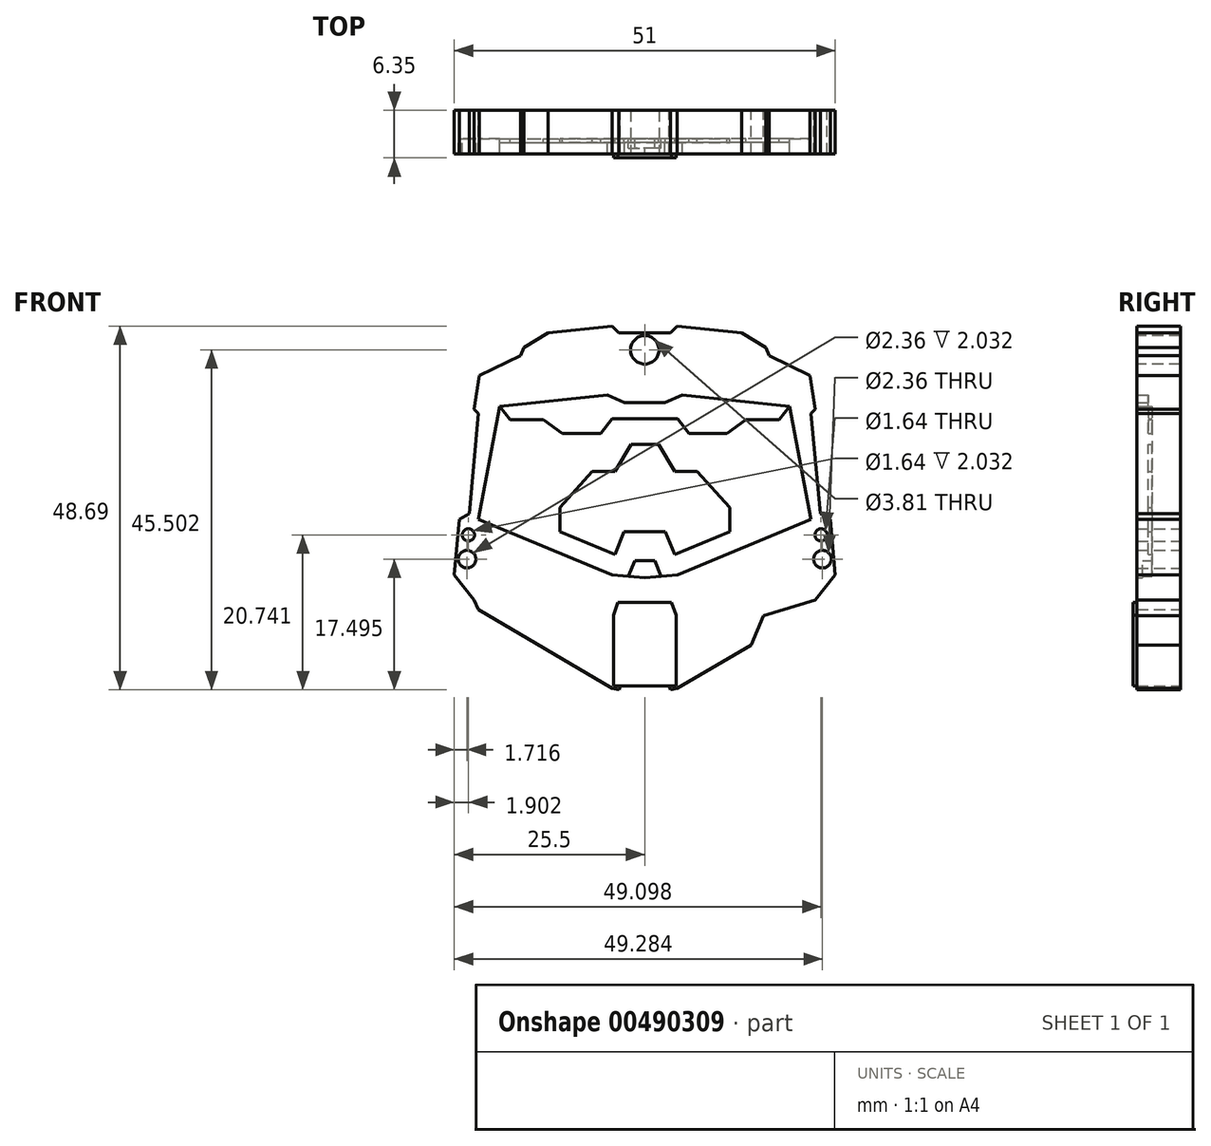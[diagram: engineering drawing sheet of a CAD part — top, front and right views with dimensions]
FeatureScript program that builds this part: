
annotation { "Feature Type Name" : "Feature", "Feature Type Description" : "" }
export const myFeature = defineFeature(function(context is Context, id is Id, definition is map)
    precondition{}
    {
        {
            var Q0;
            Q0=qCreatedBy(makeId("Front.planeOp"),FACE);
            var sketch = newSketch(context, id + "F0", { "sketchPlane" : qUnion([Q0])});
            skLineSegment(sketch, "E0", {"start": v(0, 26.6) * mm, "end": v(0, -24.2) * mm, "construction": true});
            skLineSegment(sketch, "E1", {"start": v(0, 26.6) * mm, "end": v(3.47, 26.6) * mm});
            skLineSegment(sketch, "E2", {"start": v(3.47, 26.6) * mm, "end": v(4.35, 27.52) * mm});
            skLineSegment(sketch, "E3", {"start": v(4.35, 27.52) * mm, "end": v(12.96, 26.6) * mm});
            skLineSegment(sketch, "E4", {"start": v(12.96, 26.6) * mm, "end": v(16.19, 24.61) * mm});
            skLineSegment(sketch, "E5", {"start": v(16.19, 24.61) * mm, "end": v(16.63, 23.54) * mm});
            skLineSegment(sketch, "E6", {"start": v(16.63, 23.54) * mm, "end": v(22.14, 20.88) * mm});
            skLineSegment(sketch, "E7", {"start": v(22.14, 20.88) * mm, "end": v(22.83, 16.39) * mm});
            skLineSegment(sketch, "E8", {"start": v(22.83, 16.39) * mm, "end": v(22.26, 15.82) * mm});
            skLineSegment(sketch, "E9", {"start": v(22.26, 15.82) * mm, "end": v(23.5, 2.4) * mm});
            skLineSegment(sketch, "E10", {"start": v(23.5, 2.4) * mm, "end": v(24.82, 1.66) * mm});
            skLineSegment(sketch, "E11", {"start": v(24.82, 1.66) * mm, "end": v(25.5, -5.75) * mm});
            skLineSegment(sketch, "E12", {"start": v(25.5, -5.75) * mm, "end": v(22.83, -9.12) * mm});
            skLineSegment(sketch, "E13", {"start": v(22.83, -9.12) * mm, "end": v(22.26, -10.43) * mm});
            skLineSegment(sketch, "E14", {"start": v(22.26, -10.43) * mm, "end": v(4.35, -20.92) * mm});
            skLineSegment(sketch, "E15", {"start": v(4.35, -20.92) * mm, "end": v(3.42, -21.17) * mm});
            skLineSegment(sketch, "E16", {"start": v(3.42, -21.17) * mm, "end": v(3.28, -20.63) * mm});
            skLineSegment(sketch, "E17", {"start": v(3.28, -20.63) * mm, "end": v(0, -20.63) * mm});
            skLineSegment(sketch, "E18.MirrorCS", {"start": v(-4.35, -20.92) * mm, "end": v(-3.42, -21.17) * mm});
            skLineSegment(sketch, "E19.MirrorCS", {"start": v(-3.42, -21.17) * mm, "end": v(-3.28, -20.63) * mm});
            skLineSegment(sketch, "E20.MirrorCS", {"start": v(-22.83, -9.12) * mm, "end": v(-22.26, -10.43) * mm});
            skLineSegment(sketch, "E21.MirrorCS", {"start": v(-23.5, 2.4) * mm, "end": v(-24.82, 1.66) * mm});
            skLineSegment(sketch, "E22.MirrorCS", {"start": v(-3.47, 26.6) * mm, "end": v(-4.35, 27.52) * mm});
            skLineSegment(sketch, "E23.MirrorCS", {"start": v(-16.19, 24.61) * mm, "end": v(-16.63, 23.54) * mm});
            skLineSegment(sketch, "E24.MirrorCS", {"start": v(-22.83, 16.39) * mm, "end": v(-22.26, 15.82) * mm});
            skLineSegment(sketch, "E25.MirrorCS", {"start": v(-22.26, -10.43) * mm, "end": v(-4.35, -20.92) * mm});
            skLineSegment(sketch, "E26.MirrorCS", {"start": v(-25.5, -5.75) * mm, "end": v(-22.83, -9.12) * mm});
            skLineSegment(sketch, "E27.MirrorCS", {"start": v(-24.82, 1.66) * mm, "end": v(-25.5, -5.75) * mm});
            skLineSegment(sketch, "E28.MirrorCS", {"start": v(-22.26, 15.82) * mm, "end": v(-23.5, 2.4) * mm});
            skLineSegment(sketch, "E29.MirrorCS", {"start": v(-4.35, 27.52) * mm, "end": v(-12.96, 26.6) * mm});
            skLineSegment(sketch, "E30.MirrorCS", {"start": v(-12.96, 26.6) * mm, "end": v(-16.19, 24.61) * mm});
            skLineSegment(sketch, "E31.MirrorCS", {"start": v(-16.63, 23.54) * mm, "end": v(-22.14, 20.88) * mm});
            skLineSegment(sketch, "E32.MirrorCS", {"start": v(-22.14, 20.88) * mm, "end": v(-22.83, 16.39) * mm});
            skLineSegment(sketch, "E33.MirrorCS", {"start": v(0, 26.6) * mm, "end": v(-3.47, 26.6) * mm});
            skLineSegment(sketch, "E34.MirrorCS", {"start": v(-3.28, -20.63) * mm, "end": v(0, -20.63) * mm});
            skLineSegment(sketch, "E35", {"start": v(-14.22, -15.15) * mm, "end": v(-15.87, -11.25) * mm});
            skLineSegment(sketch, "E36", {"start": v(-15.87, -11.25) * mm, "end": v(-22.83, -9.12) * mm});
            skLineSegment(sketch, "E37", {"start": v(-24.82, 1.66) * mm, "end": v(24.82, 1.66) * mm, "construction": true});
            skLineSegment(sketch, "E38", {"start": v(-22.14, 20.88) * mm, "end": v(-5, 22.7) * mm});
            skLineSegment(sketch, "E39", {"start": v(-5, 22.7) * mm, "end": v(-2.7, 21.68) * mm});
            skLineSegment(sketch, "E40", {"start": v(-2.7, 21.68) * mm, "end": v(0, 21.68) * mm});
            skLineSegment(sketch, "E41", {"start": v(-22.83, 16.39) * mm, "end": v(-5, 18.28) * mm});
            skLineSegment(sketch, "E42", {"start": v(-5, 18.28) * mm, "end": v(-2.7, 17.27) * mm});
            skLineSegment(sketch, "E43", {"start": v(-2.7, 17.27) * mm, "end": v(0, 17.27) * mm});
            skLineSegment(sketch, "E44", {"start": v(-19.4, 16.75) * mm, "end": v(-22.26, 1.66) * mm});
            skLineSegment(sketch, "E45", {"start": v(-22.26, 1.66) * mm, "end": v(-4.4, -5.75) * mm});
            skLineSegment(sketch, "E46", {"start": v(-4.4, -5.75) * mm, "end": v(0, -6.16) * mm});
            skLineSegment(sketch, "E47", {"start": v(-2.2, -5.96) * mm, "end": v(-1.33, -3.87) * mm});
            skLineSegment(sketch, "E48", {"start": v(-1.33, -3.87) * mm, "end": v(0, -3.87) * mm});
            skLineSegment(sketch, "E49", {"start": v(-4.35, -20.92) * mm, "end": v(-4.18, -20.63) * mm});
            skLineSegment(sketch, "E50", {"start": v(-4.18, -20.63) * mm, "end": v(-3.28, -20.63) * mm});
            skLineSegment(sketch, "E51", {"start": v(-12.03, -15.15) * mm, "end": v(-6.88, -10.3) * mm});
            skLineSegment(sketch, "E52", {"start": v(-6.88, -10.3) * mm, "end": v(-4.18, -11.2) * mm});
            skLineSegment(sketch, "E53", {"start": v(-4.18, -11.2) * mm, "end": v(-4.18, -20.63) * mm});
            skLineSegment(sketch, "E54", {"start": v(-4.18, -11.2) * mm, "end": v(-3.6, -9.47) * mm});
            skLineSegment(sketch, "E55", {"start": v(-3.6, -9.47) * mm, "end": v(0, -9.47) * mm});
            skLineSegment(sketch, "E56", {"start": v(-3.6, -9.47) * mm, "end": v(-6.5, -8.26) * mm});
            skLineSegment(sketch, "E57", {"start": v(-23.5, 2.4) * mm, "end": v(-22.26, 1.66) * mm});
            skLineSegment(sketch, "E58", {"start": v(-24.82, 1.66) * mm, "end": v(-22.26, 1.66) * mm});
            skLineSegment(sketch, "E59", {"start": v(-22.26, 1.66) * mm, "end": v(-22.26, -6.84) * mm});
            skLineSegment(sketch, "E60", {"start": v(-22.26, -6.84) * mm, "end": v(-22.83, -9.12) * mm});
            skCircle(sketch, "E61", {"center": v(-23.6, -0.43) * mm, "radius": 0.82 * mm});
            skCircle(sketch, "E62", {"center": v(-23.78, -3.68) * mm, "radius": 1.18 * mm});
            skLineSegment(sketch, "E63", {"start": v(-19.4, 16.75) * mm, "end": v(-18.01, 15.01) * mm});
            skLineSegment(sketch, "E64", {"start": v(-18.01, 15.01) * mm, "end": v(-13.57, 15.01) * mm});
            skLineSegment(sketch, "E65", {"start": v(-13.57, 15.01) * mm, "end": v(-11.01, 13.13) * mm});
            skLineSegment(sketch, "E66", {"start": v(-11.01, 13.13) * mm, "end": v(-5.9, 13.13) * mm});
            skLineSegment(sketch, "E67", {"start": v(-5.9, 13.13) * mm, "end": v(-4.4, 15.09) * mm});
            skLineSegment(sketch, "E68", {"start": v(-4.4, 15.09) * mm, "end": v(0, 15.09) * mm});
            skLineSegment(sketch, "E69", {"start": v(-4.02, -3.05) * mm, "end": v(-2.75, 0) * mm});
            skLineSegment(sketch, "E70", {"start": v(-2.75, 0) * mm, "end": v(0, 0) * mm});
            skLineSegment(sketch, "E71", {"start": v(-4.02, -3.05) * mm, "end": v(-11.36, 0) * mm});
            skLineSegment(sketch, "E72", {"start": v(-11.36, 0) * mm, "end": v(-11.36, 3.27) * mm});
            skLineSegment(sketch, "E73", {"start": v(-11.36, 3.27) * mm, "end": v(-7.03, 8.09) * mm});
            skLineSegment(sketch, "E74", {"start": v(-7.03, 8.09) * mm, "end": v(-4.02, 8.09) * mm});
            skLineSegment(sketch, "E75", {"start": v(-4.02, 8.09) * mm, "end": v(-1.83, 11.7) * mm});
            skLineSegment(sketch, "E76", {"start": v(-1.83, 11.7) * mm, "end": v(0, 11.7) * mm});
            skLineSegment(sketch, "E77.MirrorCS", {"start": v(4.35, -20.92) * mm, "end": v(4.18, -20.63) * mm});
            skLineSegment(sketch, "E78.MirrorCS", {"start": v(4.18, -20.63) * mm, "end": v(3.28, -20.63) * mm});
            skLineSegment(sketch, "E79.MirrorCS", {"start": v(24.82, 1.66) * mm, "end": v(22.26, 1.66) * mm});
            skLineSegment(sketch, "E80.MirrorCS", {"start": v(23.5, 2.4) * mm, "end": v(22.26, 1.66) * mm});
            skLineSegment(sketch, "E81.MirrorCS", {"start": v(22.26, -6.84) * mm, "end": v(22.83, -9.12) * mm});
            skLineSegment(sketch, "E82.MirrorCS", {"start": v(4.18, -11.2) * mm, "end": v(3.6, -9.47) * mm});
            skLineSegment(sketch, "E83.MirrorCS", {"start": v(3.6, -9.47) * mm, "end": v(0, -9.47) * mm});
            skLineSegment(sketch, "E84.MirrorCS", {"start": v(5, 18.28) * mm, "end": v(2.7, 17.27) * mm});
            skLineSegment(sketch, "E85.MirrorCS", {"start": v(7.03, 8.09) * mm, "end": v(4.02, 8.09) * mm});
            skLineSegment(sketch, "E86.MirrorCS", {"start": v(5.9, 13.13) * mm, "end": v(4.4, 15.09) * mm});
            skLineSegment(sketch, "E87.MirrorCS", {"start": v(2.75, 0) * mm, "end": v(0, 0) * mm});
            skLineSegment(sketch, "E88.MirrorCS", {"start": v(5, 22.7) * mm, "end": v(2.7, 21.68) * mm});
            skLineSegment(sketch, "E89.MirrorCS", {"start": v(19.4, 16.75) * mm, "end": v(18.01, 15.01) * mm});
            skLineSegment(sketch, "E90.MirrorCS", {"start": v(4.4, 15.09) * mm, "end": v(0, 15.09) * mm});
            skLineSegment(sketch, "E91.MirrorCS", {"start": v(6.88, -10.3) * mm, "end": v(4.18, -11.2) * mm});
            skLineSegment(sketch, "E92.MirrorCS", {"start": v(18.01, 15.01) * mm, "end": v(13.57, 15.01) * mm});
            skLineSegment(sketch, "E93.MirrorCS", {"start": v(4.4, -5.75) * mm, "end": v(0, -6.16) * mm});
            skLineSegment(sketch, "E94.MirrorCS", {"start": v(4.02, -3.05) * mm, "end": v(2.75, 0) * mm});
            skLineSegment(sketch, "E95.MirrorCS", {"start": v(11.36, 0) * mm, "end": v(11.36, 3.27) * mm});
            skLineSegment(sketch, "E96.MirrorCS", {"start": v(3.6, -9.47) * mm, "end": v(6.5, -8.26) * mm});
            skLineSegment(sketch, "E97.MirrorCS", {"start": v(2.7, 21.68) * mm, "end": v(0, 21.68) * mm});
            skLineSegment(sketch, "E98.MirrorCS", {"start": v(2.7, 17.27) * mm, "end": v(0, 17.27) * mm});
            skLineSegment(sketch, "E99.MirrorCS", {"start": v(4.02, 8.09) * mm, "end": v(1.83, 11.7) * mm});
            skLineSegment(sketch, "E100.MirrorCS", {"start": v(13.57, 15.01) * mm, "end": v(11.01, 13.13) * mm});
            skCircle(sketch, "E101.MirrorC", {"center": v(23.78, -3.68) * mm, "radius": 1.18 * mm});
            skLineSegment(sketch, "E102.MirrorCS", {"start": v(22.26, 1.66) * mm, "end": v(22.26, -6.84) * mm});
            skLineSegment(sketch, "E103.MirrorCS", {"start": v(14.22, -15.15) * mm, "end": v(15.87, -11.25) * mm});
            skCircle(sketch, "E104.MirrorC", {"center": v(23.6, -0.43) * mm, "radius": 0.82 * mm});
            skLineSegment(sketch, "E105.MirrorCS", {"start": v(11.01, 13.13) * mm, "end": v(5.9, 13.13) * mm});
            skLineSegment(sketch, "E106.MirrorCS", {"start": v(11.36, 3.27) * mm, "end": v(7.03, 8.09) * mm});
            skLineSegment(sketch, "E107.MirrorCS", {"start": v(22.83, 16.39) * mm, "end": v(5, 18.28) * mm});
            skLineSegment(sketch, "E108.MirrorCS", {"start": v(4.02, -3.05) * mm, "end": v(11.36, 0) * mm});
            skLineSegment(sketch, "E109.MirrorCS", {"start": v(22.26, 1.66) * mm, "end": v(4.4, -5.75) * mm});
            skLineSegment(sketch, "E110.MirrorCS", {"start": v(15.87, -11.25) * mm, "end": v(22.83, -9.12) * mm});
            skLineSegment(sketch, "E111.MirrorCS", {"start": v(19.4, 16.75) * mm, "end": v(22.26, 1.66) * mm});
            skLineSegment(sketch, "E112.MirrorCS", {"start": v(22.14, 20.88) * mm, "end": v(5, 22.7) * mm});
            skLineSegment(sketch, "E113.MirrorCS", {"start": v(12.03, -15.15) * mm, "end": v(6.88, -10.3) * mm});
            skLineSegment(sketch, "E114.MirrorCS", {"start": v(4.18, -11.2) * mm, "end": v(4.18, -20.63) * mm});
            skLineSegment(sketch, "E115.MirrorCS", {"start": v(24.82, 1.66) * mm, "end": v(-24.82, 1.66) * mm, "construction": true});
            skLineSegment(sketch, "E116.MirrorCS", {"start": v(1.33, -3.87) * mm, "end": v(0, -3.87) * mm});
            skLineSegment(sketch, "E117.MirrorCS", {"start": v(2.2, -5.96) * mm, "end": v(1.33, -3.87) * mm});
            skLineSegment(sketch, "E118.MirrorCS", {"start": v(1.83, 11.7) * mm, "end": v(0, 11.7) * mm});
            skLineSegment(sketch, "E119", {"start": v(-19.4, 16.75) * mm, "end": v(-22.26, 15.82) * mm});
            skLineSegment(sketch, "E120", {"start": v(19.4, 16.75) * mm, "end": v(22.26, 15.82) * mm});
            skSolve(sketch);
        }
        {
            var Q0;
            Q0=makeQuery(id+"F0.imprint","IMPRINT",FACE,{"disambiguationData":[TD([[makeQuery(id+"F0.imprint","IMPRINT",EDGE,{"derivedFrom":sQuery(id+"F0.wireOp",EDGE,"E18.MirrorCS")}),1.0]])]});
            var Q1;
            Q1=makeQuery(id+"F0.imprint","IMPRINT",FACE,{"disambiguationData":[TD([[makeQuery(id+"F0.imprint","IMPRINT",EDGE,{"derivedFrom":sQuery(id+"F0.wireOp",EDGE,"E16")}),-1.0]])]});
            var Q2;
            {var subQ1=sQuery(id+"F0.wireOp",EDGE,"E35");Q2=makeQuery(id+"F0.imprint","IMPRINT",FACE,{"disambiguationData":[TD([[makeQuery(id+"F0.imprint","IMPRINT",EDGE,{"derivedFrom":subQ1}),-1.0]])]});}
            var Q3;
            {var subQ0=sQuery(id+"F0.wireOp",EDGE,"E20.MirrorCS");Q3=makeQuery(id+"F0.imprint","IMPRINT",FACE,{"disambiguationData":[TD([[makeQuery(id+"F0.imprint","IMPRINT",EDGE,{"derivedFrom":subQ0}),1.0]])]});}
            var Q4;
            {var subQ0=sQuery(id+"F0.wireOp",EDGE,"E13");Q4=makeQuery(id+"F0.imprint","IMPRINT",FACE,{"disambiguationData":[TD([[makeQuery(id+"F0.imprint","IMPRINT",EDGE,{"derivedFrom":subQ0}),-1.0]])]});}
            var Q5;
            Q5=makeQuery(id+"F0.imprint","IMPRINT",FACE,{"disambiguationData":[TD([[makeQuery(id+"F0.imprint","IMPRINT",EDGE,{"derivedFrom":sQuery(id+"F0.wireOp",EDGE,"E79.MirrorCS")}),1.0]])]});
            var Q6;
            Q6=makeQuery(id+"F0.imprint","IMPRINT",FACE,{"disambiguationData":[TD([[makeQuery(id+"F0.imprint","IMPRINT",EDGE,{"derivedFrom":sQuery(id+"F0.wireOp",EDGE,"E26.MirrorCS")}),1.0]])]});
            var Q7;
            Q7=makeQuery(id+"F0.imprint","IMPRINT",FACE,{"disambiguationData":[TD([[makeQuery(id+"F0.imprint","IMPRINT",EDGE,{"derivedFrom":sQuery(id+"F0.wireOp",EDGE,"E28.MirrorCS")}),1.0]])]});
            var Q8;
            Q8=makeQuery(id+"F0.imprint","IMPRINT",FACE,{"disambiguationData":[TD([[makeQuery(id+"F0.imprint","IMPRINT",EDGE,{"derivedFrom":sQuery(id+"F0.wireOp",EDGE,"E80.MirrorCS")}),-1.0]])]});
            var Q9;
            Q9=makeQuery(id+"F0.imprint","IMPRINT",FACE,{"disambiguationData":[TD([[makeQuery(id+"F0.imprint","IMPRINT",EDGE,{"derivedFrom":sQuery(id+"F0.wireOp",EDGE,"E79.MirrorCS")}),-1.0]])]});
            var Q10;
            Q10=makeQuery(id+"F0.imprint","IMPRINT",FACE,{"disambiguationData":[TD([[makeQuery(id+"F0.imprint","IMPRINT",EDGE,{"derivedFrom":sQuery(id+"F0.wireOp",EDGE,"E21.MirrorCS")}),1.0]])]});
            var Q11;
            {var subQ0=sQuery(id+"F0.wireOp",EDGE,"E24.MirrorCS");Q11=makeQuery(id+"F0.imprint","IMPRINT",FACE,{"disambiguationData":[TD([[makeQuery(id+"F0.imprint","IMPRINT",EDGE,{"derivedFrom":subQ0}),1.0]])]});}
            var Q12;
            {var subQ0=sQuery(id+"F0.wireOp",EDGE,"E8");Q12=makeQuery(id+"F0.imprint","IMPRINT",FACE,{"disambiguationData":[TD([[makeQuery(id+"F0.imprint","IMPRINT",EDGE,{"derivedFrom":subQ0}),-1.0]])]});}
            var Q13;
            {var subQ4=sQuery(id+"F0.wireOp",EDGE,"E32.MirrorCS");Q13=makeQuery(id+"F0.imprint","IMPRINT",FACE,{"disambiguationData":[TD([[makeQuery(id+"F0.imprint","IMPRINT",EDGE,{"derivedFrom":subQ4}),1.0]])]});}
            var Q14;
            Q14=makeQuery(id+"F0.imprint","IMPRINT",FACE,{"disambiguationData":[TD([[makeQuery(id+"F0.imprint","IMPRINT",EDGE,{"derivedFrom":sQuery(id+"F0.wireOp",EDGE,"E22.MirrorCS")}),1.0]])]});
            extrude(context, id + "F1", {"entities" : qUnion([Q0, Q1, Q2, Q3, Q4, Q5, Q6, Q7, Q8, Q9, Q10, Q11, Q12, Q13, Q14]), "depth" : 5.84 * mm});
        }
        {
            var Q0;
            Q0=makeQuery(id+"F0.imprint","IMPRINT",FACE,{"disambiguationData":[TD([[makeQuery(id+"F0.imprint","IMPRINT",EDGE,{"derivedFrom":sQuery(id+"F0.wireOp",EDGE,"E101.MirrorC")}),-1.0]])]});
            var Q1;
            Q1=makeQuery(id+"F0.imprint","IMPRINT",FACE,{"disambiguationData":[TD([[makeQuery(id+"F0.imprint","IMPRINT",EDGE,{"derivedFrom":sQuery(id+"F0.wireOp",EDGE,"E104.MirrorC")}),-1.0]])]});
            var Q2;
            Q2=makeQuery(id+"F0.imprint","IMPRINT",FACE,{"disambiguationData":[TD([[makeQuery(id+"F0.imprint","IMPRINT",EDGE,{"derivedFrom":sQuery(id+"F0.wireOp",EDGE,"E62")}),1.0]])]});
            var Q3;
            Q3=makeQuery(id+"F0.imprint","IMPRINT",FACE,{"disambiguationData":[TD([[makeQuery(id+"F0.imprint","IMPRINT",EDGE,{"derivedFrom":sQuery(id+"F0.wireOp",EDGE,"E61")}),1.0]])]});
            var Q4;
            Q4=makeQuery(id+"F0.imprint","IMPRINT",FACE,{"disambiguationData":[TD([[makeQuery(id+"F0.imprint","IMPRINT",EDGE,{"derivedFrom":sQuery(id+"F0.wireOp",EDGE,"E44")}),1.0]])]});
            extrude(context, id + "F2", {"entities" : qUnion([Q0, Q1, Q2, Q3, Q4]), "operationType" : NewBodyOperationType.ADD, "depth" : 3.8 * mm});
        }
        {
            var Q0;
            {var subQ4=sQuery(id+"F0.wireOp",EDGE,"E47");Q0=makeQuery(id+"F0.imprint","IMPRINT",FACE,{"disambiguationData":[TD([[makeQuery(id+"F0.imprint","IMPRINT",EDGE,{"derivedFrom":subQ4}),-1.0]])]});}
            extrude(context, id + "F3", {"entities" : qUnion([Q0]), "operationType" : NewBodyOperationType.ADD, "depth" : 5.08 * mm});
        }
        {
            var Q0;
            Q0=makeQuery(id+"F0.imprint","IMPRINT",FACE,{"disambiguationData":[TD([[makeQuery(id+"F0.imprint","IMPRINT",EDGE,{"derivedFrom":sQuery(id+"F0.wireOp",EDGE,"E69")}),1.0]])]});
            var Q1;
            {var subQ1=sQuery(id+"F0.wireOp",EDGE,"E42");Q1=makeQuery(id+"F0.imprint","IMPRINT",FACE,{"disambiguationData":[TD([[makeQuery(id+"F0.imprint","IMPRINT",EDGE,{"derivedFrom":subQ1}),-1.0]])]});}
            extrude(context, id + "F4", {"entities" : qUnion([Q0, Q1]), "operationType" : NewBodyOperationType.ADD, "depth" : 4.32 * mm});
        }
        {
            var Q0;
            Q0=makeQuery(id+"F1.opExtrude","CAP_FACE",FACE,{"disambiguationData":[OSD([sQuery(id+"F0.wireOp",EDGE,"E18.MirrorCS"),sQuery(id+"F0.wireOp",EDGE,"E19.MirrorCS"),sQuery(id+"F0.wireOp",EDGE,"E20.MirrorCS"),sQuery(id+"F0.wireOp",EDGE,"E21.MirrorCS"),sQuery(id+"F0.wireOp",EDGE,"E22.MirrorCS"),sQuery(id+"F0.wireOp",EDGE,"E23.MirrorCS"),sQuery(id+"F0.wireOp",EDGE,"E24.MirrorCS"),sQuery(id+"F0.wireOp",EDGE,"E25.MirrorCS"),sQuery(id+"F0.wireOp",EDGE,"E26.MirrorCS"),sQuery(id+"F0.wireOp",EDGE,"E27.MirrorCS"),sQuery(id+"F0.wireOp",EDGE,"E28.MirrorCS"),sQuery(id+"F0.wireOp",EDGE,"E29.MirrorCS"),sQuery(id+"F0.wireOp",EDGE,"E30.MirrorCS"),sQuery(id+"F0.wireOp",EDGE,"E31.MirrorCS"),sQuery(id+"F0.wireOp",EDGE,"E32.MirrorCS"),sQuery(id+"F0.wireOp",EDGE,"E33.MirrorCS"),sQuery(id+"F0.wireOp",EDGE,"E34.MirrorCS"),sQuery(id+"F0.wireOp",EDGE,"E41"),sQuery(id+"F0.wireOp",EDGE,"E42"),sQuery(id+"F0.wireOp",EDGE,"E43"),sQuery(id+"F0.wireOp",EDGE,"E44"),sQuery(id+"F0.wireOp",EDGE,"E45"),sQuery(id+"F0.wireOp",EDGE,"E46"),sQuery(id+"F0.wireOp",EDGE,"E61"),sQuery(id+"F0.wireOp",EDGE,"E62"),sQuery(id+"F0.wireOp",EDGE,"E16"),sQuery(id+"F0.wireOp",EDGE,"E17"),sQuery(id+"F0.wireOp",EDGE,"E15"),sQuery(id+"F0.wireOp",EDGE,"E10"),sQuery(id+"F0.wireOp",EDGE,"E13"),sQuery(id+"F0.wireOp",EDGE,"E8"),sQuery(id+"F0.wireOp",EDGE,"E84.MirrorCS"),sQuery(id+"F0.wireOp",EDGE,"E12"),sQuery(id+"F0.wireOp",EDGE,"E2"),sQuery(id+"F0.wireOp",EDGE,"E1"),sQuery(id+"F0.wireOp",EDGE,"E93.MirrorCS"),sQuery(id+"F0.wireOp",EDGE,"E4"),sQuery(id+"F0.wireOp",EDGE,"E98.MirrorCS"),sQuery(id+"F0.wireOp",EDGE,"E5"),sQuery(id+"F0.wireOp",EDGE,"E101.MirrorC"),sQuery(id+"F0.wireOp",EDGE,"E11"),sQuery(id+"F0.wireOp",EDGE,"E104.MirrorC"),sQuery(id+"F0.wireOp",EDGE,"E14"),sQuery(id+"F0.wireOp",EDGE,"E107.MirrorCS"),sQuery(id+"F0.wireOp",EDGE,"E109.MirrorCS"),sQuery(id+"F0.wireOp",EDGE,"E3"),sQuery(id+"F0.wireOp",EDGE,"E6"),sQuery(id+"F0.wireOp",EDGE,"E111.MirrorCS"),sQuery(id+"F0.wireOp",EDGE,"E9"),sQuery(id+"F0.wireOp",EDGE,"E7")])],"isStart":false});
            var sketch = newSketch(context, id + "F5", { "sketchPlane" : qUnion([Q0])});
            skCircle(sketch, "E121", {"center": v(0, 24.33) * mm, "radius": 1.9 * mm});
            skSolve(sketch);
        }
        {
            var Q0;
            Q0 = qSketchRegion(id + "F5", true);
            extrude(context, id + "F6", {"entities" : qUnion([Q0]), "operationType" : NewBodyOperationType.REMOVE, "oppositeDirection" : true, "depth" : 25.4 * mm});
        }
        {
            var Q0;
            Q0=makeQuery(id+"F0.imprint","IMPRINT",FACE,{"disambiguationData":[TD([[makeQuery(id+"F0.imprint","IMPRINT",EDGE,{"derivedFrom":sQuery(id+"F0.wireOp",EDGE,"E34.MirrorCS")}),1.0]])]});
            extrude(context, id + "F7", {"entities" : qUnion([Q0]), "operationType" : NewBodyOperationType.ADD, "depth" : 6.35 * mm});
        }
    });
